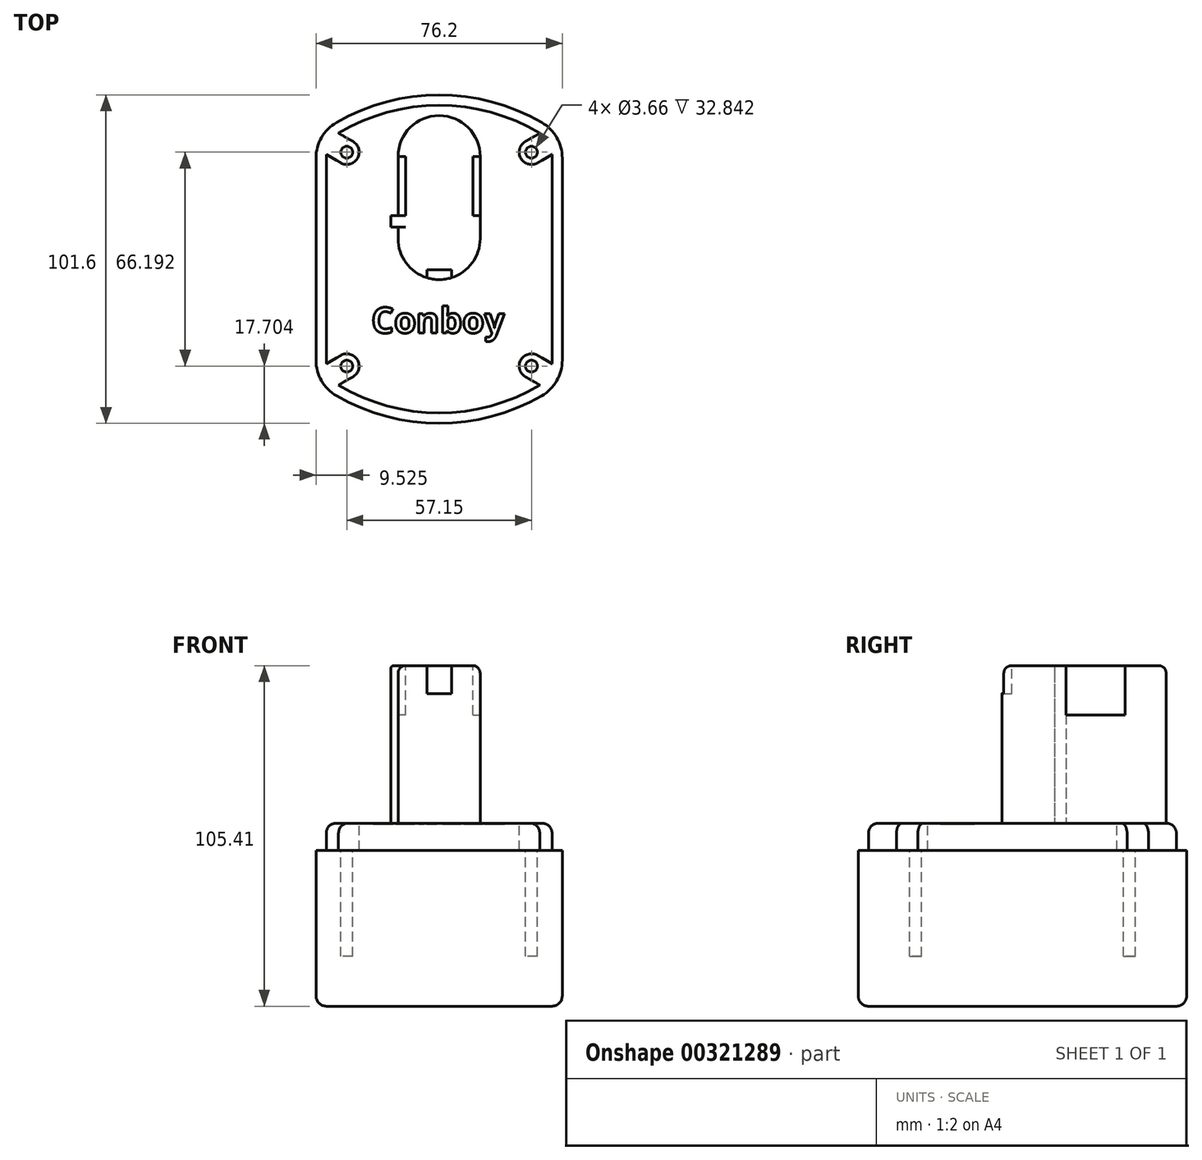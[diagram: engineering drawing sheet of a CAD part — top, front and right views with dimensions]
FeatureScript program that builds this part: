
annotation { "Feature Type Name" : "Feature", "Feature Type Description" : "" }
export const myFeature = defineFeature(function(context is Context, id is Id, definition is map)
    precondition{}
    {
        {
            var Q0;
            Q0=qCreatedBy(makeId("Top.planeOp"),FACE);
            var sketch = newSketch(context, id + "F0", { "sketchPlane" : qUnion([Q0])});
            skLineSegment(sketch, "E0.bottom", {"start": v(38.1, 38.1) * mm, "end": v(-38.1, 38.1) * mm, "construction": true});
            skLineSegment(sketch, "E0.top", {"start": v(38.1, -38.1) * mm, "end": v(-38.1, -38.1) * mm, "construction": true});
            skLineSegment(sketch, "E0.left", {"start": v(38.1, 38.1) * mm, "end": v(38.1, -38.1) * mm});
            skLineSegment(sketch, "E0.right", {"start": v(-38.1, 38.1) * mm, "end": v(-38.1, -38.1) * mm});
            skPoint(sketch, "E0.middle", {"position": v(0, 0) * mm});
            skLineSegment(sketch, "E1", {"start": v(0, 38.1) * mm, "end": v(0, 50.8) * mm, "construction": true});
            skPoint(sketch, "E1.endSnap0", {"position": v(0, 38.1) * mm});
            skArc(sketch, "E2", {"start": v(38.1, 38.1) * mm, "mid": v(0, 50.8) * mm, "end": v(-38.1, 38.1) * mm});
            skLineSegment(sketch, "E3", {"start": v(-38.1, 0) * mm, "end": v(38.1, 0) * mm, "construction": true});
            skArc(sketch, "E4.MirrorCS", {"start": v(38.1, -38.1) * mm, "mid": v(0, -50.8) * mm, "end": v(-38.1, -38.1) * mm});
            skSolve(sketch);
        }
        {
            var Q0;
            Q0 = qSketchRegion(id + "F0", true);
            extrude(context, id + "F1", {"entities" : qUnion([Q0]), "oppositeDirection" : true, "depth" : 48.26 * mm});
        }
        {
            var Q0;
            Q0=makeQuery(id+"F1.opExtrude","CAP_FACE",FACE,{"disambiguationData":[OSD([sQuery(id+"F0.wireOp",EDGE,"E0.left"),sQuery(id+"F0.wireOp",EDGE,"E0.right"),sQuery(id+"F0.wireOp",EDGE,"E2"),sQuery(id+"F0.wireOp",EDGE,"E4.MirrorCS")])],"isStart":true});
            var sketch = newSketch(context, id + "F2", { "sketchPlane" : qUnion([Q0])});
            skArc(sketch, "E5.0.0", {"start": v(38.1, 38.1) * mm, "mid": v(0, 50.8) * mm, "end": v(-38.1, 38.1) * mm, "construction": true});
            skLineSegment(sketch, "E5.0.1", {"start": v(-38.1, 38.1) * mm, "end": v(-38.1, -38.1) * mm, "construction": true});
            skArc(sketch, "E5.0.2", {"start": v(-38.1, -38.1) * mm, "mid": v(0, -50.8) * mm, "end": v(38.1, -38.1) * mm, "construction": true});
            skLineSegment(sketch, "E5.0.3", {"start": v(38.1, -38.1) * mm, "end": v(38.1, 38.1) * mm, "construction": true});
            skArc(sketch, "E6.0", {"start": v(34.92, 36.49) * mm, "mid": v(0, 47.63) * mm, "end": v(-34.92, 36.49) * mm});
            skLineSegment(sketch, "E6.1", {"start": v(34.92, -36.49) * mm, "end": v(34.92, 36.49) * mm});
            skArc(sketch, "E6.2", {"start": v(-34.92, -36.49) * mm, "mid": v(0, -47.62) * mm, "end": v(34.93, -36.49) * mm});
            skLineSegment(sketch, "E6.3", {"start": v(-34.92, 36.49) * mm, "end": v(-34.92, -36.49) * mm});
            skSolve(sketch);
        }
        {
            var Q0;
            Q0 = qSketchRegion(id + "F2", true);
            extrude(context, id + "F3", {"entities" : qUnion([Q0]), "operationType" : NewBodyOperationType.ADD, "depth" : 8.38 * mm});
        }
        {
            var Q0;
            Q0=makeQuery(id+"F3.opExtrude","CAP_FACE",FACE,{"disambiguationData":[OSD([sQuery(id+"F2.wireOp",EDGE,"E6.0"),sQuery(id+"F2.wireOp",EDGE,"E6.1"),sQuery(id+"F2.wireOp",EDGE,"E6.2"),sQuery(id+"F2.wireOp",EDGE,"E6.3")])],"isStart":false});
            var sketch = newSketch(context, id + "F4", { "sketchPlane" : qUnion([Q0])});
            skLineSegment(sketch, "E7.bottom", {"start": v(-28.57, 33.1) * mm, "end": v(28.58, 33.1) * mm, "construction": true});
            skLineSegment(sketch, "E7.top", {"start": v(-28.58, -33.1) * mm, "end": v(28.57, -33.1) * mm, "construction": true});
            skLineSegment(sketch, "E7.left", {"start": v(-28.57, 33.1) * mm, "end": v(-28.58, -33.1) * mm, "construction": true});
            skLineSegment(sketch, "E7.right", {"start": v(28.58, 33.1) * mm, "end": v(28.57, -33.1) * mm, "construction": true});
            skPoint(sketch, "E7.middle", {"position": v(0, 0) * mm});
            skLineSegment(sketch, "E8", {"start": v(-28.58, -33.1) * mm, "end": v(-50.57, -45.8) * mm, "construction": true});
            skArc(sketch, "E9.0.startCap", {"start": v(-30.48, -29.8) * mm, "mid": v(-25.28, -31.2) * mm, "end": v(-26.67, -36.4) * mm});
            skArc(sketch, "E9.0.endCap", {"start": v(-48.67, -49.1) * mm, "mid": v(-53.87, -47.7) * mm, "end": v(-52.48, -42.5) * mm});
            skLineSegment(sketch, "E9.0.left", {"start": v(-26.67, -36.4) * mm, "end": v(-48.67, -49.1) * mm});
            skLineSegment(sketch, "E9.0.right", {"start": v(-30.48, -29.8) * mm, "end": v(-52.48, -42.5) * mm});
            skLineSegment(sketch, "E10", {"start": v(-28.58, 0) * mm, "end": v(28.58, 0) * mm, "construction": true});
            skLineSegment(sketch, "E11", {"start": v(0, 33.1) * mm, "end": v(0, -33.1) * mm, "construction": true});
            skLineSegment(sketch, "E12.MirrorCS", {"start": v(26.67, -36.4) * mm, "end": v(48.67, -49.1) * mm});
            skArc(sketch, "E13.MirrorCS", {"start": v(30.48, -29.8) * mm, "mid": v(25.28, -31.2) * mm, "end": v(26.67, -36.4) * mm});
            skLineSegment(sketch, "E14.MirrorCS", {"start": v(30.48, -29.8) * mm, "end": v(52.48, -42.5) * mm});
            skArc(sketch, "E15.MirrorCS", {"start": v(48.67, -49.1) * mm, "mid": v(53.87, -47.7) * mm, "end": v(52.48, -42.5) * mm});
            skArc(sketch, "E16.MirrorCS", {"start": v(-30.48, 29.8) * mm, "mid": v(-25.28, 31.2) * mm, "end": v(-26.67, 36.4) * mm});
            skLineSegment(sketch, "E17.MirrorCS", {"start": v(-30.48, 29.8) * mm, "end": v(-52.48, 42.5) * mm});
            skLineSegment(sketch, "E18.MirrorCS", {"start": v(-26.67, 36.4) * mm, "end": v(-48.67, 49.1) * mm});
            skArc(sketch, "E19.MirrorCS", {"start": v(-48.67, 49.1) * mm, "mid": v(-53.87, 47.7) * mm, "end": v(-52.48, 42.5) * mm});
            skArc(sketch, "E20.MirrorCS", {"start": v(30.48, 29.8) * mm, "mid": v(25.28, 31.2) * mm, "end": v(26.67, 36.4) * mm});
            skLineSegment(sketch, "E21.MirrorCS", {"start": v(26.67, 36.4) * mm, "end": v(48.67, 49.1) * mm});
            skLineSegment(sketch, "E22.MirrorCS", {"start": v(30.48, 29.8) * mm, "end": v(52.48, 42.5) * mm});
            skArc(sketch, "E23.MirrorCS", {"start": v(48.67, 49.1) * mm, "mid": v(53.87, 47.7) * mm, "end": v(52.48, 42.5) * mm});
            skCircle(sketch, "E24", {"center": v(-28.57, 33.1) * mm, "radius": 1.83 * mm, "construction": true});
            skCircle(sketch, "E25", {"center": v(28.58, 33.1) * mm, "radius": 1.83 * mm, "construction": true});
            skCircle(sketch, "E26", {"center": v(-28.58, -33.1) * mm, "radius": 1.83 * mm, "construction": true});
            skCircle(sketch, "E27", {"center": v(28.57, -33.1) * mm, "radius": 1.83 * mm, "construction": true});
            skSolve(sketch);
        }
        {
            var Q0;
            Q0 = qSketchRegion(id + "F4", true);
            var Q1;
            Q1=makeQuery(id+"F1.opExtrude","CAP_FACE",FACE,{"disambiguationData":[OSD([sQuery(id+"F0.wireOp",EDGE,"E0.left"),sQuery(id+"F0.wireOp",EDGE,"E0.right"),sQuery(id+"F0.wireOp",EDGE,"E2"),sQuery(id+"F0.wireOp",EDGE,"E4.MirrorCS")])],"isStart":true});
            extrude(context, id + "F5", {"entities" : qUnion([Q0]), "operationType" : NewBodyOperationType.REMOVE, "endBound" : BoundingType.UP_TO_SURFACE, "oppositeDirection" : true, "endBoundEntityFace" : qUnion([Q1]), "depth" : 25.4 * mm});
        }
        {
            var Q0;
            Q0=makeQuery(id+"F5.boolean.opBoolean","MERGE",FACE,{"derivedFrom":[makeQuery(id+"F1.opExtrude","CAP_FACE",FACE,{"disambiguationData":[OSD([sQuery(id+"F0.wireOp",EDGE,"E0.left"),sQuery(id+"F0.wireOp",EDGE,"E0.right"),sQuery(id+"F0.wireOp",EDGE,"E2"),sQuery(id+"F0.wireOp",EDGE,"E4.MirrorCS")])],"isStart":true})],"fromTools":[makeQuery(id+"F5.opExtrude","CAP_FACE",FACE,{"disambiguationData":[OSD([sQuery(id+"F4.wireOp",EDGE,"E9.0.startCap"),sQuery(id+"F4.wireOp",EDGE,"E9.0.endCap"),sQuery(id+"F4.wireOp",EDGE,"E9.0.left"),sQuery(id+"F4.wireOp",EDGE,"E9.0.right")])],"isStart":false}),makeQuery(id+"F5.opExtrude","CAP_FACE",FACE,{"disambiguationData":[OSD([sQuery(id+"F4.wireOp",EDGE,"E12.MirrorCS"),sQuery(id+"F4.wireOp",EDGE,"E13.MirrorCS"),sQuery(id+"F4.wireOp",EDGE,"E14.MirrorCS"),sQuery(id+"F4.wireOp",EDGE,"E15.MirrorCS")])],"isStart":false}),makeQuery(id+"F5.opExtrude","CAP_FACE",FACE,{"disambiguationData":[OSD([sQuery(id+"F4.wireOp",EDGE,"E16.MirrorCS"),sQuery(id+"F4.wireOp",EDGE,"E17.MirrorCS"),sQuery(id+"F4.wireOp",EDGE,"E18.MirrorCS"),sQuery(id+"F4.wireOp",EDGE,"E19.MirrorCS")])],"isStart":false}),makeQuery(id+"F5.opExtrude","CAP_FACE",FACE,{"disambiguationData":[OSD([sQuery(id+"F4.wireOp",EDGE,"E20.MirrorCS"),sQuery(id+"F4.wireOp",EDGE,"E21.MirrorCS"),sQuery(id+"F4.wireOp",EDGE,"E22.MirrorCS"),sQuery(id+"F4.wireOp",EDGE,"E23.MirrorCS")])],"isStart":false})]});
            var sketch = newSketch(context, id + "F6", { "sketchPlane" : qUnion([Q0])});
            skCircle(sketch, "E28.0", {"center": v(-28.57, 33.1) * mm, "radius": 1.83 * mm});
            skCircle(sketch, "E28.1", {"center": v(28.58, 33.1) * mm, "radius": 1.83 * mm});
            skCircle(sketch, "E28.2", {"center": v(-28.58, -33.1) * mm, "radius": 1.83 * mm});
            skCircle(sketch, "E28.3", {"center": v(28.57, -33.1) * mm, "radius": 1.83 * mm});
            skSolve(sketch);
        }
        {
            var Q0;
            Q0 = qSketchRegion(id + "F6", true);
            extrude(context, id + "F7", {"entities" : qUnion([Q0]), "operationType" : NewBodyOperationType.REMOVE, "oppositeDirection" : true, "depth" : 32.84 * mm});
        }
        {
            var Q0;
            Q0=qCreatedBy(makeId("Top.planeOp"),FACE);
            var sketch = newSketch(context, id + "F8", { "sketchPlane" : qUnion([Q0])});
            skLineSegment(sketch, "E29", {"start": v(0, 6.35) * mm, "end": v(0, 31.75) * mm, "construction": true});
            skArc(sketch, "E30.0.startCap", {"start": v(12.7, 6.35) * mm, "mid": v(0, -6.35) * mm, "end": v(-12.7, 6.35) * mm});
            skArc(sketch, "E30.0.endCap", {"start": v(-12.7, 31.75) * mm, "mid": v(0, 44.45) * mm, "end": v(12.7, 31.75) * mm});
            skLineSegment(sketch, "E30.0.left", {"start": v(-12.7, 6.35) * mm, "end": v(-12.7, 31.75) * mm});
            skLineSegment(sketch, "E30.0.right", {"start": v(12.7, 6.35) * mm, "end": v(12.7, 31.75) * mm});
            skPoint(sketch, "E31", {"position": v(0, 19.05) * mm});
            skPoint(sketch, "E32", {"position": v(0, 44.45) * mm});
            skPoint(sketch, "E33", {"position": v(0, -6.35) * mm});
            skSolve(sketch);
        }
        {
            var Q0;
            Q0 = qSketchRegion(id + "F8", true);
            extrude(context, id + "F9", {"entities" : qUnion([Q0]), "operationType" : NewBodyOperationType.ADD, "depth" : 57.15 * mm});
        }
        {
            var Q0;
            Q0=makeQuery(id+"F3.opExtrude","CAP_FACE",FACE,{"disambiguationData":[OSD([sQuery(id+"F2.wireOp",EDGE,"E6.0"),sQuery(id+"F2.wireOp",EDGE,"E6.1"),sQuery(id+"F2.wireOp",EDGE,"E6.2"),sQuery(id+"F2.wireOp",EDGE,"E6.3")])],"isStart":false});
            var sketch = newSketch(context, id + "F10", { "sketchPlane" : qUnion([Q0])});
            skLineSegment(sketch, "E34.bottom", {"start": v(-12.7, 9.9) * mm, "end": v(-14.99, 9.9) * mm});
            skLineSegment(sketch, "E34.top", {"start": v(-12.7, 13.46) * mm, "end": v(-14.99, 13.46) * mm});
            skLineSegment(sketch, "E34.left", {"start": v(-12.7, 9.9) * mm, "end": v(-12.7, 13.46) * mm});
            skLineSegment(sketch, "E34.right", {"start": v(-14.99, 9.9) * mm, "end": v(-14.99, 13.46) * mm});
            skSolve(sketch);
        }
        {
            var Q0;
            Q0 = qSketchRegion(id + "F10", true);
            var Q1;
            Q1=makeQuery(id+"F9.opExtrude","CAP_FACE",FACE,{"disambiguationData":[OSD([sQuery(id+"F8.wireOp",EDGE,"E30.0.startCap"),sQuery(id+"F8.wireOp",EDGE,"E30.0.endCap"),sQuery(id+"F8.wireOp",EDGE,"E30.0.left"),sQuery(id+"F8.wireOp",EDGE,"E30.0.right")])],"isStart":false});
            extrude(context, id + "F11", {"entities" : qUnion([Q0]), "operationType" : NewBodyOperationType.ADD, "endBound" : BoundingType.UP_TO_SURFACE, "endBoundEntityFace" : qUnion([Q1]), "depth" : 25.4 * mm});
        }
        {
            var Q0;
            Q0=makeQuery(id+"F9.opExtrude","CAP_EDGE",EDGE,{"disambiguationData":[OSD([sQuery(id+"F8.wireOp",EDGE,"E30.0.right")])],"isStart":false});
            fillet(context, id + "F12", {"entities" : qUnion([Q0]), "radius" : 2.3 * mm, "tangentPropagation" : true, "allowEdgeOverflow" : false});
        }
        {
            var Q0;
            Q0=makeQuery(id+"F11.boolean.opBoolean","MERGE",FACE,{"derivedFrom":[makeQuery(id+"F9.opExtrude","CAP_FACE",FACE,{"disambiguationData":[OSD([sQuery(id+"F8.wireOp",EDGE,"E30.0.startCap"),sQuery(id+"F8.wireOp",EDGE,"E30.0.endCap"),sQuery(id+"F8.wireOp",EDGE,"E30.0.left"),sQuery(id+"F8.wireOp",EDGE,"E30.0.right")])],"isStart":false}),makeQuery(id+"F11.opExtrude","CAP_FACE",FACE,{"disambiguationData":[OSD([sQuery(id+"F10.wireOp",EDGE,"E34.bottom"),sQuery(id+"F10.wireOp",EDGE,"E34.top"),sQuery(id+"F10.wireOp",EDGE,"E34.left"),sQuery(id+"F10.wireOp",EDGE,"E34.right")])],"isStart":false})]});
            var sketch = newSketch(context, id + "F13", { "sketchPlane" : qUnion([Q0])});
            skLineSegment(sketch, "E35.bottom", {"start": v(10.41, 31.75) * mm, "end": v(12.7, 31.75) * mm});
            skLineSegment(sketch, "E35.top", {"start": v(10.41, 13.46) * mm, "end": v(12.7, 13.46) * mm});
            skLineSegment(sketch, "E35.left", {"start": v(10.41, 31.75) * mm, "end": v(10.41, 13.46) * mm});
            skLineSegment(sketch, "E35.right", {"start": v(12.7, 31.75) * mm, "end": v(12.7, 13.46) * mm});
            skLineSegment(sketch, "E36.0", {"start": v(0, 6.35) * mm, "end": v(0, 31.75) * mm, "construction": true});
            skLineSegment(sketch, "E37.MirrorCS", {"start": v(-10.41, 31.75) * mm, "end": v(-12.7, 31.75) * mm});
            skLineSegment(sketch, "E38.MirrorCS", {"start": v(-12.7, 31.75) * mm, "end": v(-12.7, 13.46) * mm});
            skLineSegment(sketch, "E39.MirrorCS", {"start": v(-10.41, 31.75) * mm, "end": v(-10.41, 13.46) * mm});
            skLineSegment(sketch, "E40.MirrorCS", {"start": v(-10.41, 13.46) * mm, "end": v(-12.7, 13.46) * mm});
            skArc(sketch, "E41.0", {"start": v(3.81, -5.77) * mm, "mid": v(0, -6.35) * mm, "end": v(-3.81, -5.77) * mm, "construction": true});
            skArc(sketch, "E42.0", {"start": v(-10.41, 6.35) * mm, "mid": v(0, -4.06) * mm, "end": v(10.41, 6.35) * mm, "construction": true});
            skLineSegment(sketch, "E43", {"start": v(-3.81, -5.77) * mm, "end": v(-3.81, -3.34) * mm, "construction": true});
            skLineSegment(sketch, "E44", {"start": v(-3.81, -3.34) * mm, "end": v(3.81, -3.34) * mm, "construction": true});
            skLineSegment(sketch, "E45", {"start": v(3.81, -3.34) * mm, "end": v(3.81, -5.77) * mm, "construction": true});
            skPoint(sketch, "E46.orphan", {"position": v(12.7, 6.35) * mm});
            skPoint(sketch, "E47.orphan", {"position": v(-12.7, 6.35) * mm});
            skSolve(sketch);
        }
        {
            var Q0;
            Q0 = qSketchRegion(id + "F13", true);
            extrude(context, id + "F14", {"entities" : qUnion([Q0]), "operationType" : NewBodyOperationType.REMOVE, "oppositeDirection" : true, "depth" : 15.24 * mm});
        }
        {
            var Q0;
            {var subQ7=sQuery(id+"F13.wireOp",EDGE,"E35.left");Q0=makeQuery(id+"F13.imprint","IMPRINT",FACE,{"disambiguationData":[TD([[makeQuery(id+"F13.imprint","IMPRINT",EDGE,{"derivedFrom":subQ7}),1.0]])]});}
            var sketch = newSketch(context, id + "F15", { "sketchPlane" : qUnion([Q0])});
            skLineSegment(sketch, "E48.0", {"start": v(-3.81, -5.77) * mm, "end": v(-3.81, -3.34) * mm});
            skLineSegment(sketch, "E48.1", {"start": v(-3.81, -3.34) * mm, "end": v(3.81, -3.34) * mm});
            skLineSegment(sketch, "E48.2", {"start": v(3.81, -3.34) * mm, "end": v(3.81, -5.77) * mm});
            skArc(sketch, "E48.3", {"start": v(3.8, -5.77) * mm, "mid": v(0, -6.35) * mm, "end": v(-3.81, -5.77) * mm});
            skPoint(sketch, "E49.orphan", {"position": v(-12.7, 6.35) * mm});
            skPoint(sketch, "E50.orphan", {"position": v(12.7, 6.35) * mm});
            skSolve(sketch);
        }
        {
            var Q0;
            Q0 = qSketchRegion(id + "F15", true);
            extrude(context, id + "F16", {"entities" : qUnion([Q0]), "operationType" : NewBodyOperationType.REMOVE, "oppositeDirection" : true, "depth" : 8.64 * mm});
        }
        {
            var Q0;
            Q0=makeQuery(id+"F11.opExtrude","CAP_EDGE",EDGE,{"disambiguationData":[OSD([sQuery(id+"F10.wireOp",EDGE,"E34.right")])],"isStart":false});
            fillet(context, id + "F17", {"entities" : qUnion([Q0]), "radius" : 1.02 * mm, "tangentPropagation" : true, "allowEdgeOverflow" : false});
        }
        {
            var Q0;
            Q0=makeQuery(id+"F3.opExtrude","CAP_FACE",FACE,{"disambiguationData":[OSD([sQuery(id+"F2.wireOp",EDGE,"E6.0"),sQuery(id+"F2.wireOp",EDGE,"E6.1"),sQuery(id+"F2.wireOp",EDGE,"E6.2"),sQuery(id+"F2.wireOp",EDGE,"E6.3")])],"isStart":false});
            var sketch = newSketch(context, id + "F18", { "sketchPlane" : qUnion([Q0])});
            skText(sketch, "E51", { "text": "Conboy", "fontName": "OpenSans-Bold.ttf"});
            skArc(sketch, "E52.0", {"start": v(38.1, -38.1) * mm, "mid": v(0, -50.8) * mm, "end": v(-38.1, -38.1) * mm});
            skLineSegment(sketch, "E53", {"start": v(0, -50.8) * mm, "end": v(0, -22.86) * mm, "construction": true});
            skPoint(sketch, "E53.endSnap0", {"position": v(0, -47.62) * mm});
            const initialGuessF18  = {"E51": [-0.02098, -0.02286, 1, 0, 0.00795]};
            skSetInitialGuess(sketch, initialGuessF18);
            skSolve(sketch);
        }
        {
            var Q0;
            Q0 = qSketchRegion(id + "F18", true);
            extrude(context, id + "F19", {"entities" : qUnion([Q0]), "operationType" : NewBodyOperationType.REMOVE, "oppositeDirection" : true, "depth" : 0.25 * mm});
        }
        {
            var Q0;
            Q0=makeQuery(id+"F1.opExtrude","SWEPT_EDGE",EDGE,{"disambiguationData":[OSD([sQuery(id+"F0.wireOp",EDGE,"E0.left"),sQuery(id+"F0.wireOp",EDGE,"E4.MirrorCS")])]});
            var Q1;
            Q1=makeQuery(id+"F1.opExtrude","SWEPT_EDGE",EDGE,{"disambiguationData":[OSD([sQuery(id+"F0.wireOp",EDGE,"E0.left"),sQuery(id+"F0.wireOp",EDGE,"E2")])]});
            var Q2;
            Q2=makeQuery(id+"F1.opExtrude","SWEPT_EDGE",EDGE,{"disambiguationData":[OSD([sQuery(id+"F0.wireOp",EDGE,"E0.right"),sQuery(id+"F0.wireOp",EDGE,"E4.MirrorCS")])]});
            var Q3;
            Q3=makeQuery(id+"F1.opExtrude","SWEPT_EDGE",EDGE,{"disambiguationData":[OSD([sQuery(id+"F0.wireOp",EDGE,"E0.right"),sQuery(id+"F0.wireOp",EDGE,"E2")])]});
            fillet(context, id + "F20", {"entities" : qUnion([Q0, Q1, Q2, Q3]), "radius" : 12.7 * mm, "tangentPropagation" : true, "allowEdgeOverflow" : false});
        }
        {
            var Q0;
            Q0=makeQuery(id+"F3.opExtrude","CAP_EDGE",EDGE,{"disambiguationData":[OSD([sQuery(id+"F2.wireOp",EDGE,"E6.2")])],"isStart":false});
            var Q1;
            Q1=makeQuery(id+"F3.opExtrude","CAP_EDGE",EDGE,{"disambiguationData":[OSD([sQuery(id+"F2.wireOp",EDGE,"E6.1")])],"isStart":false});
            var Q2;
            Q2=makeQuery(id+"F3.opExtrude","CAP_EDGE",EDGE,{"disambiguationData":[OSD([sQuery(id+"F2.wireOp",EDGE,"E6.0")])],"isStart":false});
            var Q3;
            Q3=makeQuery(id+"F3.opExtrude","CAP_EDGE",EDGE,{"disambiguationData":[OSD([sQuery(id+"F2.wireOp",EDGE,"E6.3")])],"isStart":false});
            fillet(context, id + "F21", {"entities" : qUnion([Q0, Q1, Q2, Q3]), "radius" : 3.05 * mm, "tangentPropagation" : true, "allowEdgeOverflow" : false});
        }
        {
            var Q0;
            Q0=makeQuery(id+"F1.opExtrude","CAP_EDGE",EDGE,{"disambiguationData":[OSD([sQuery(id+"F0.wireOp",EDGE,"E0.left")])],"isStart":false});
            fillet(context, id + "F22", {"entities" : qUnion([Q0]), "radius" : 3.17 * mm, "tangentPropagation" : true, "allowEdgeOverflow" : false});
        }
    });
